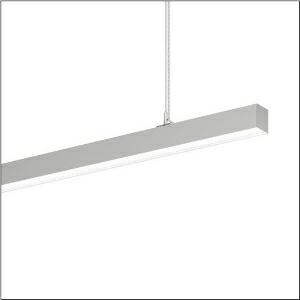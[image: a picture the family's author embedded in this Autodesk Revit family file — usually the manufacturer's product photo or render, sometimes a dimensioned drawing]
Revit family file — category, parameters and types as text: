
# Revit family: silica_21_51mx33tctds
name_source: partatom
category: Lighting Fixtures
units: mm (PartAtom-declared; Revit-internal decimal feet)

## family parameters
Cut with Voids When Loaded = No
Host = Face
Light Source = No
Part Type = Normal
Room Calculation Point = No
Round Connector Dimension = Use Diameter
Shared = No

## types (1)
- --- (1 x LED, 14340 lm, 134.7 W, 6500K)
    Apparent Load = 135 VA
    CIE Flux Codes = 78 96 99 56 100
    Color Rendering = 80
    Color Temperature = 6500K
    Default Elevation = 1800 mm
    Description = Silica 21, office luminaire, primary optical cover: prismatic diffuser, of PMMA, CAT 2 (L<= 3000cd/m²), light emission: direct/indirect distribution, primary light characteristic: symmetric, installation type: suspended mounting, LED, rated luminous flux: 14.340lm, luminous efficacy: 101lm/W, light colour: 8tw, colour temperature: 2700..6500K, control gear: DALI DT8, with terminal, 3+2-pole, max. 2.5mm², mains connection: 220..240V, AC, 50/60Hz, rated input power: 141.4W, luminaire housing, of aluminium, metallic grey (RAL 9006), length: 3.004mm, width: 53mm, height: 53mm, protection rating (complete): IP20, insulation class (complete): insulation class I (protective earthing), certification: CE, permissible operating ambient temperature: 0..+35°C, standard: EN 50419, packaging unit: 1 piece
    Height = 53 mm
    Lamp = 1 x LED
    Lamp Light Flux = 14340 lm
    Lamp Power = 134.7 W
    Lamp count = 1
    Length = 3004 mm
    Luminous efficacy = 106 lm/W
    Manufacturer = Siteco
    ModVariant = No
    Model = 51MX33TCTDS
    Mounting Place = Ceiling
    Mounting Type = Pendant
    Number of Poles = 1
    OnlyDefault = Yes
    Power Factor = 1
    Product Name = Silica 21
    Product group = office luminaire | ceiling pendant
    ProductGroupID = 903
    Protection Class = Protection class I
    Protection Degree = IP 20
    RLX_Detail_Level = 1
    RLX_Emergency_Light_Flux = 0 lm
    RLX_Emergency_Type = 0
    RLX_Emergency_Type_DB = No
    RlxData = <blob elided: 20081 chars, md5=7acffa92>
    Socket = socket
    Standby Power = 0 W
    System Light Flux = 14340 lm
    System Power = 135 W
    Type Comments = individual setting
    Type Image = l_1335864.jpg
    URL = http://relux.com
    VarID = @adj_139229
    Voltage = 0 V
    Weight = 0.00 kg
    Width = 53 mm

## geometry (parser evidence)
native form markers: Blend x4, Sweep x12
no freeform markers — native parametric forms only
